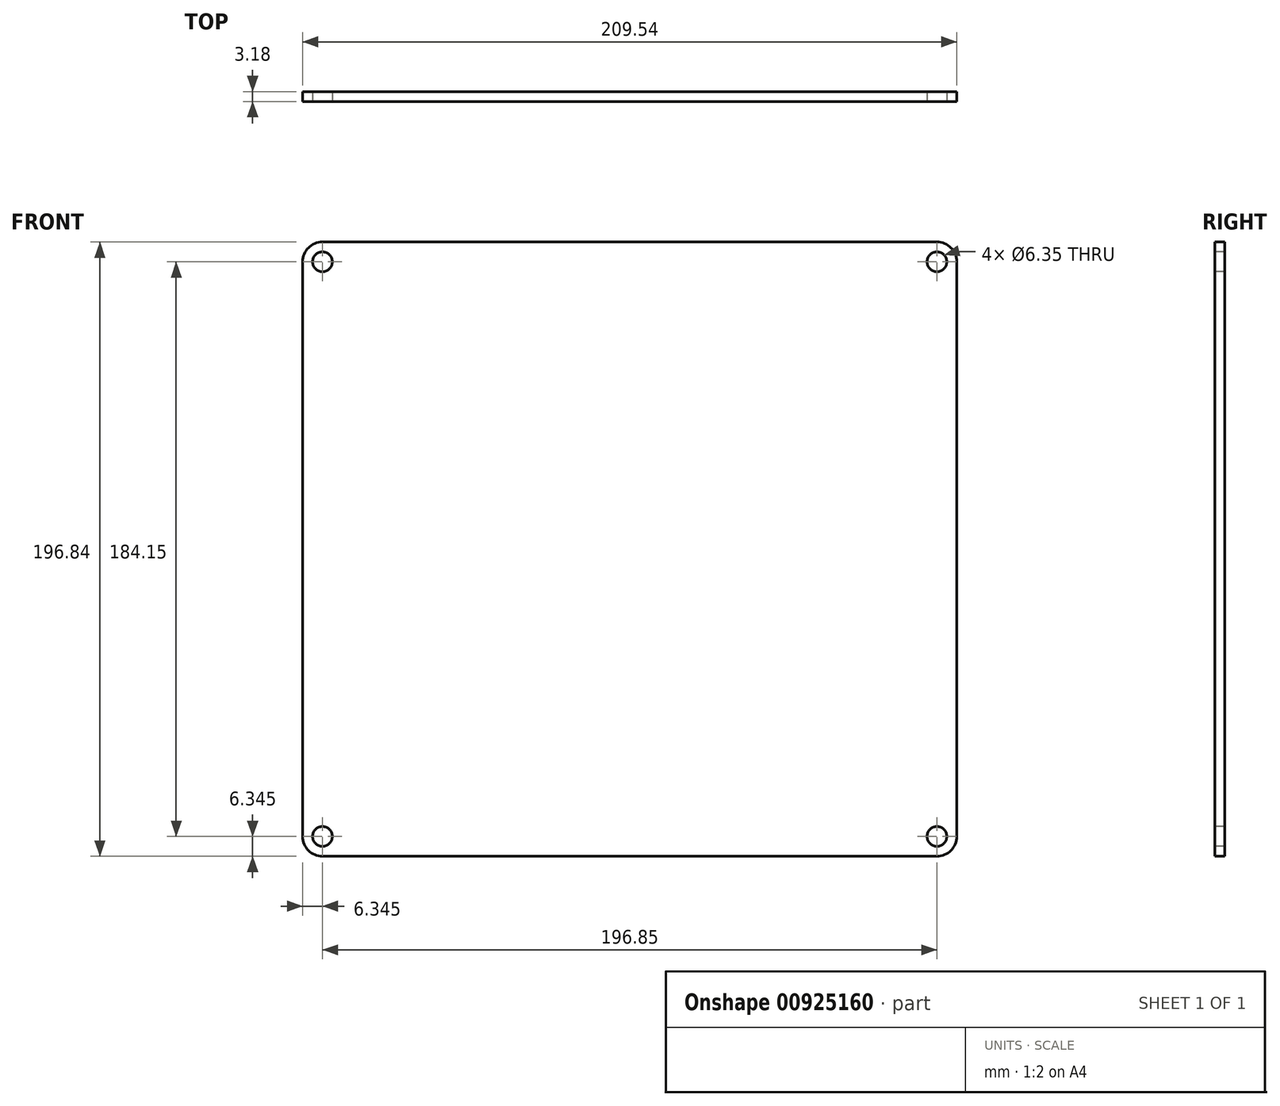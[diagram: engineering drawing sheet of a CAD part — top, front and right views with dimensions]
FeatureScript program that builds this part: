
annotation { "Feature Type Name" : "Feature", "Feature Type Description" : "" }
export const myFeature = defineFeature(function(context is Context, id is Id, definition is map)
    precondition{}
    {
        {
            var Q0;
            Q0=qCreatedBy(makeId("Front.planeOp"),FACE);
            var sketch = newSketch(context, id + "F0", { "sketchPlane" : qUnion([Q0])});
            skLineSegment(sketch, "E0.bottom", {"start": v(-98.43, 98.42) * mm, "end": v(98.43, 98.43) * mm});
            skLineSegment(sketch, "E0.top", {"start": v(-98.43, -98.43) * mm, "end": v(98.43, -98.43) * mm});
            skLineSegment(sketch, "E0.left", {"start": v(-104.78, 92.08) * mm, "end": v(-104.78, -92.08) * mm});
            skLineSegment(sketch, "E0.right", {"start": v(104.78, 92.08) * mm, "end": v(104.78, -92.08) * mm});
            skPoint(sketch, "E1.visualSharp", {"position": v(-104.78, 98.42) * mm});
            skArc(sketch, "E1.filletArc", {"start": v(-98.43, 98.42) * mm, "mid": v(-102.92, 96.57) * mm, "end": v(-104.77, 92.08) * mm});
            skPoint(sketch, "E2.visualSharp", {"position": v(104.78, 98.43) * mm});
            skArc(sketch, "E2.filletArc", {"start": v(104.77, 92.08) * mm, "mid": v(102.92, 96.57) * mm, "end": v(98.43, 98.42) * mm});
            skPoint(sketch, "E3.visualSharp", {"position": v(104.78, -98.43) * mm});
            skArc(sketch, "E3.filletArc", {"start": v(98.43, -98.43) * mm, "mid": v(102.92, -96.57) * mm, "end": v(104.78, -92.08) * mm});
            skPoint(sketch, "E4.visualSharp", {"position": v(-104.78, -98.43) * mm});
            skArc(sketch, "E4.filletArc", {"start": v(-104.78, -92.08) * mm, "mid": v(-102.92, -96.57) * mm, "end": v(-98.43, -98.43) * mm});
            skSolve(sketch);
        }
        {
            var Q0;
            Q0 = qSketchRegion(id + "F0", true);
            extrude(context, id + "F1", {"entities" : qUnion([Q0]), "depth" : 3.17 * mm, "offsetDistance" : 25.4 * mm});
        }
        {
            var Q0;
            Q0=makeQuery(id+"F1.opExtrude","CAP_FACE",FACE,{"disambiguationData":[OSD([sQuery(id+"F0.wireOp",EDGE,"E0.bottom"),sQuery(id+"F0.wireOp",EDGE,"E0.top"),sQuery(id+"F0.wireOp",EDGE,"E0.left"),sQuery(id+"F0.wireOp",EDGE,"E0.right"),sQuery(id+"F0.wireOp",EDGE,"E1.filletArc"),sQuery(id+"F0.wireOp",EDGE,"E2.filletArc"),sQuery(id+"F0.wireOp",EDGE,"E3.filletArc"),sQuery(id+"F0.wireOp",EDGE,"E4.filletArc")])],"isStart":false});
            var sketch = newSketch(context, id + "F2", { "sketchPlane" : qUnion([Q0])});
            skCircle(sketch, "E5", {"center": v(-98.42, 92.08) * mm, "radius": 3.18 * mm});
            skCircle(sketch, "E6", {"center": v(98.42, 92.08) * mm, "radius": 3.18 * mm});
            skCircle(sketch, "E7", {"center": v(98.43, -92.08) * mm, "radius": 3.18 * mm});
            skCircle(sketch, "E8", {"center": v(-98.42, -92.08) * mm, "radius": 3.18 * mm});
            skSolve(sketch);
        }
        {
            var Q0;
            Q0 = qSketchRegion(id + "F2", true);
            extrude(context, id + "F3", {"entities" : qUnion([Q0]), "operationType" : NewBodyOperationType.REMOVE, "oppositeDirection" : true, "depth" : 25.4 * mm, "offsetDistance" : 25.4 * mm});
        }
    });
